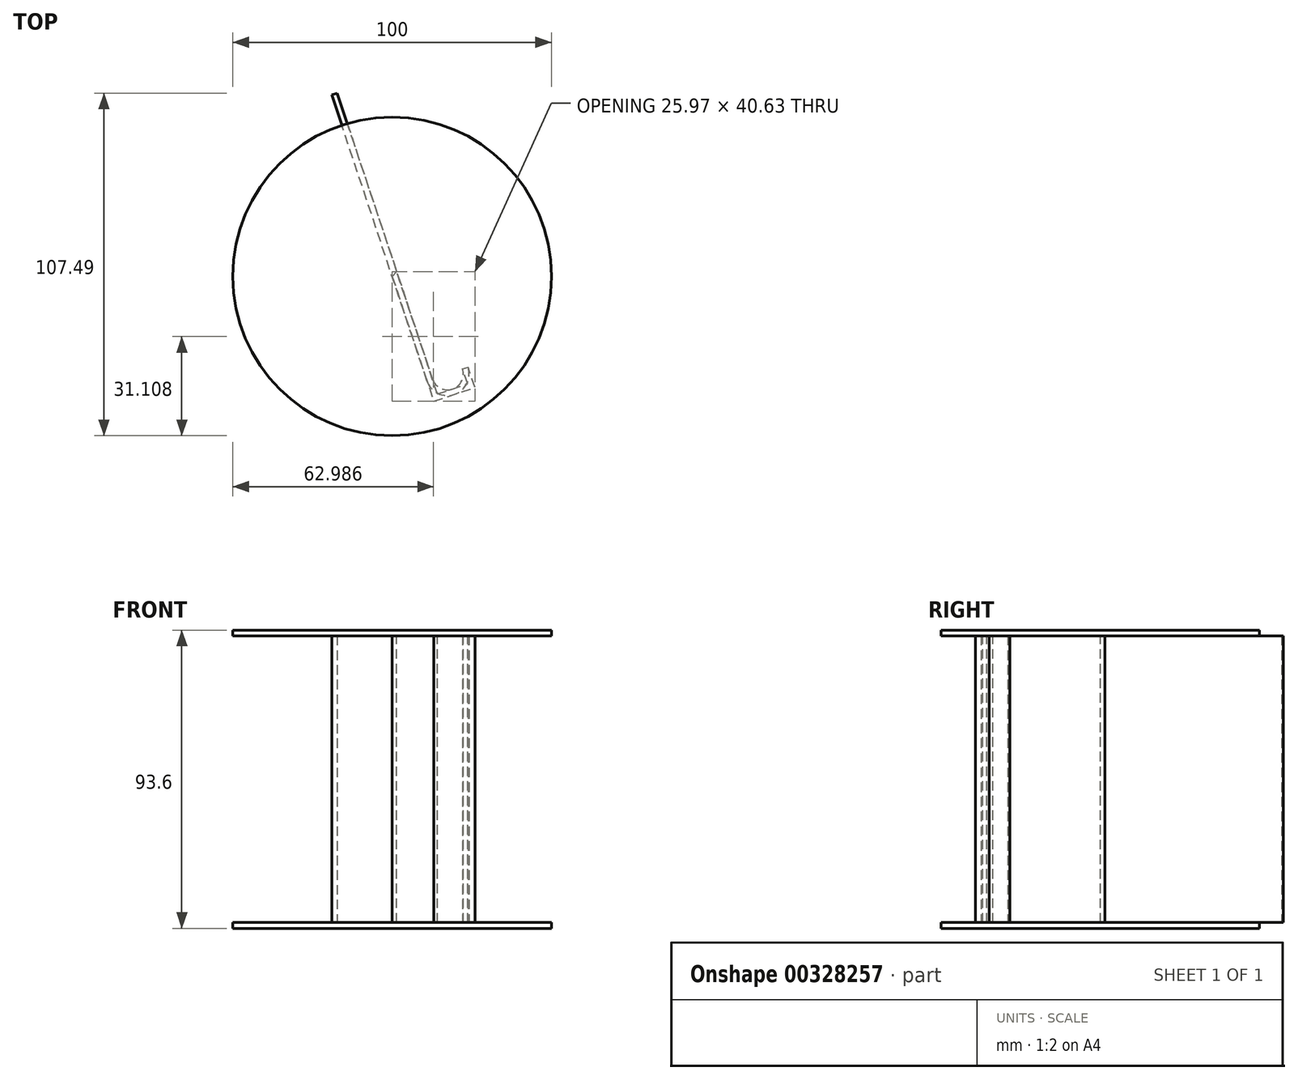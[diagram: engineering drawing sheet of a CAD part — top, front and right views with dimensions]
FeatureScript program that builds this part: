
annotation { "Feature Type Name" : "Feature", "Feature Type Description" : "" }
export const myFeature = defineFeature(function(context is Context, id is Id, definition is map)
    precondition{}
    {
        {
            var Q0;
            Q0=qCreatedBy(makeId("Top.planeOp"),FACE);
            var sketch = newSketch(context, id + "F0", { "sketchPlane" : qUnion([Q0])});
            skCircle(sketch, "E0", {"center": v(0, 0) * mm, "radius": 50 * mm});
            skLineSegment(sketch, "E1", {"start": v(0, -50) * mm, "end": v(50, 0) * mm});
            skLineSegment(sketch, "E2", {"start": v(25, -25) * mm, "end": v(0, -50) * mm});
            skLineSegment(sketch, "E3", {"start": v(12.5, -37.5) * mm, "end": v(0, 0) * mm});
            skLineSegment(sketch, "E4", {"start": v(-50, 0) * mm, "end": v(0, -50) * mm});
            skLineSegment(sketch, "E5", {"start": v(50, 0) * mm, "end": v(0, 50) * mm});
            skLineSegment(sketch, "E6", {"start": v(-25, -25) * mm, "end": v(25, 25) * mm});
            skLineSegment(sketch, "E7", {"start": v(25, 25) * mm, "end": v(0, 0) * mm});
            skLineSegment(sketch, "E8", {"start": v(25, 25) * mm, "end": v(12.5, 12.5) * mm});
            skLineSegment(sketch, "E9", {"start": v(0, 0) * mm, "end": v(1.27, 1.27) * mm});
            skLineSegment(sketch, "E10", {"start": v(12.5, -37.5) * mm, "end": v(13.77, -36.23) * mm});
            skLineSegment(sketch, "E11", {"start": v(12.5, -37.5) * mm, "end": v(14.2, -36.93) * mm});
            skLineSegment(sketch, "E12", {"start": v(0, 0) * mm, "end": v(1.7, 0.57) * mm});
            skLineSegment(sketch, "E13", {"start": v(1.7, 0.57) * mm, "end": v(14.2, -36.93) * mm});
            skLineSegment(sketch, "E14", {"start": v(1.7, 0.57) * mm, "end": v(1.42, 1.42) * mm});
            skLineSegment(sketch, "E15", {"start": v(14.2, -36.93) * mm, "end": v(23.7, -33.77) * mm});
            skLineSegment(sketch, "E16", {"start": v(12.5, -37.5) * mm, "end": v(13.07, -39.2) * mm});
            skLineSegment(sketch, "E17", {"start": v(13.07, -39.2) * mm, "end": v(24.26, -35.48) * mm});
            skLineSegment(sketch, "E18", {"start": v(23.7, -33.77) * mm, "end": v(24.26, -35.48) * mm});
            skLineSegment(sketch, "E19", {"start": v(24.26, -35.48) * mm, "end": v(25.97, -34.9) * mm});
            skLineSegment(sketch, "E20", {"start": v(25.97, -34.9) * mm, "end": v(23.82, -28.46) * mm});
            skLineSegment(sketch, "E21", {"start": v(23.7, -33.77) * mm, "end": v(22.11, -29.03) * mm});
            skLineSegment(sketch, "E22", {"start": v(22.11, -29.03) * mm, "end": v(23.82, -28.46) * mm});
            skLineSegment(sketch, "E23", {"start": v(23.7, -33.77) * mm, "end": v(25.4, -33.2) * mm});
            skLineSegment(sketch, "E24", {"start": v(0, 0) * mm, "end": v(-18.97, 56.92) * mm});
            skLineSegment(sketch, "E25", {"start": v(-18.97, 56.92) * mm, "end": v(-17.27, 57.5) * mm});
            skLineSegment(sketch, "E26", {"start": v(-17.27, 57.5) * mm, "end": v(1.42, 1.42) * mm});
            skSolve(sketch);
        }
        {
            var Q0;
            {var subQ0=sQuery(id+"F0.wireOp",EDGE,"E5");var subQ1=sQuery(id+"F0.wireOp",EDGE,"E0");var subQ3=makeQuery(id+"F0.imprint","INTERSECT",VERTEX,{"derivedFrom":[subQ1,subQ0]});Q0=makeQuery(id+"F0.imprint","IMPRINT",FACE,{"disambiguationData":[TD([[makeQuery(id+"F0.imprint","IMPRINT",EDGE,{"disambiguationData":[TD([[subQ3,1.0]])],"derivedFrom":subQ0}),-1.0]])]});}
            var Q1;
            {var subQ7=sQuery(id+"F0.wireOp",EDGE,"E14");Q1=makeQuery(id+"F0.imprint","IMPRINT",FACE,{"disambiguationData":[TD([[makeQuery(id+"F0.imprint","IMPRINT",EDGE,{"derivedFrom":subQ7}),-1.0]])]});}
            var Q2;
            {var subQ1=sQuery(id+"F0.wireOp",EDGE,"E6");var subQ3=makeQuery(id+"F0.imprint","IMPRINT",VERTEX,{"disambiguationData":[OD(0.0)],"derivedFrom":subQ1});Q2=makeQuery(id+"F0.imprint","IMPRINT",FACE,{"disambiguationData":[TD([[makeQuery(id+"F0.imprint","IMPRINT",EDGE,{"disambiguationData":[TD([[subQ3,-1.0]])],"derivedFrom":subQ1}),1.0]])]});}
            var Q3;
            {var subQ7=sQuery(id+"F0.wireOp",EDGE,"E15");Q3=makeQuery(id+"F0.imprint","IMPRINT",FACE,{"disambiguationData":[TD([[makeQuery(id+"F0.imprint","IMPRINT",EDGE,{"derivedFrom":subQ7}),1.0]])]});}
            var Q4;
            Q4=makeQuery(id+"F0.imprint","IMPRINT",FACE,{"disambiguationData":[TD([[makeQuery(id+"F0.imprint","IMPRINT",EDGE,{"derivedFrom":sQuery(id+"F0.wireOp",EDGE,"E21")}),-1.0]])]});
            var Q5;
            Q5=makeQuery(id+"F0.imprint","IMPRINT",FACE,{"disambiguationData":[TD([[makeQuery(id+"F0.imprint","IMPRINT",EDGE,{"derivedFrom":sQuery(id+"F0.wireOp",EDGE,"E18")}),1.0]])]});
            var Q6;
            Q6=makeQuery(id+"F0.imprint","IMPRINT",FACE,{"disambiguationData":[TD([[makeQuery(id+"F0.imprint","IMPRINT",EDGE,{"derivedFrom":sQuery(id+"F0.wireOp",EDGE,"E11")}),-1.0]])]});
            var Q7;
            {var subQ1=sQuery(id+"F0.wireOp",EDGE,"E3");Q7=makeQuery(id+"F0.imprint","IMPRINT",FACE,{"disambiguationData":[TD([[makeQuery(id+"F0.imprint","IMPRINT",EDGE,{"derivedFrom":subQ1}),-1.0]])]});}
            var Q8;
            {var subQ0=sQuery(id+"F0.wireOp",EDGE,"E11");Q8=makeQuery(id+"F0.imprint","IMPRINT",FACE,{"disambiguationData":[TD([[makeQuery(id+"F0.imprint","IMPRINT",EDGE,{"derivedFrom":subQ0}),1.0]])]});}
            var Q9;
            {var subQ0=sQuery(id+"F0.wireOp",EDGE,"E3");Q9=makeQuery(id+"F0.imprint","IMPRINT",FACE,{"disambiguationData":[TD([[makeQuery(id+"F0.imprint","IMPRINT",EDGE,{"derivedFrom":subQ0}),1.0]])]});}
            var Q10;
            {var subQ3=sQuery(id+"F0.wireOp",EDGE,"E0");var subQ5=sQuery(id+"F0.wireOp",EDGE,"E26");var subQ8=makeQuery(id+"F0.imprint","INTERSECT",VERTEX,{"derivedFrom":[subQ3,subQ5]});Q10=makeQuery(id+"F0.imprint","IMPRINT",FACE,{"disambiguationData":[TD([[makeQuery(id+"F0.imprint","IMPRINT",EDGE,{"disambiguationData":[TD([[subQ8,-1.0]])],"derivedFrom":subQ3}),1.0]])]});}
            var Q11;
            {var subQ0=sQuery(id+"F0.wireOp",EDGE,"E12");Q11=makeQuery(id+"F0.imprint","IMPRINT",FACE,{"disambiguationData":[TD([[makeQuery(id+"F0.imprint","IMPRINT",EDGE,{"derivedFrom":subQ0}),1.0]])]});}
            var Q12;
            {var subQ0=sQuery(id+"F0.wireOp",EDGE,"E4");var subQ1=sQuery(id+"F0.wireOp",EDGE,"E0");var subQ2=makeQuery(id+"F0.imprint","INTERSECT",VERTEX,{"derivedFrom":[subQ1,subQ0]});Q12=makeQuery(id+"F0.imprint","IMPRINT",FACE,{"disambiguationData":[TD([[makeQuery(id+"F0.imprint","IMPRINT",EDGE,{"disambiguationData":[TD([[subQ2,1.0]])],"derivedFrom":subQ1}),1.0]])]});}
            var Q13;
            {var subQ0=sQuery(id+"F0.wireOp",EDGE,"E4");var subQ1=sQuery(id+"F0.wireOp",EDGE,"E0");var subQ2=makeQuery(id+"F0.imprint","INTERSECT",VERTEX,{"derivedFrom":[subQ1,subQ0]});Q13=makeQuery(id+"F0.imprint","IMPRINT",FACE,{"disambiguationData":[TD([[makeQuery(id+"F0.imprint","IMPRINT",EDGE,{"disambiguationData":[TD([[subQ2,-1.0]])],"derivedFrom":subQ0}),-1.0]])]});}
            extrude(context, id + "F1", {"entities" : qUnion([Q0, Q1, Q2, Q3, Q4, Q5, Q6, Q7, Q8, Q9, Q10, Q11, Q12, Q13]), "depth" : (45 + 1.8) * mm, "offsetDistance" : 25 * mm, "hasSecondDirection" : true, "secondDirectionOppositeDirection" : true, "secondDirectionDepth" : 46.8 * mm});
        }
        {
            var Q0;
            {var subQ0=sQuery(id+"F0.wireOp",EDGE,"E4");var subQ1=sQuery(id+"F0.wireOp",EDGE,"E0");var subQ2=makeQuery(id+"F0.imprint","INTERSECT",VERTEX,{"derivedFrom":[subQ1,subQ0]});var subQ5=sQuery(id+"F0.wireOp",EDGE,"E6");var subQ7=makeQuery(id+"F0.imprint","IMPRINT",EDGE,{"disambiguationData":[TD([[subQ2,-1.0]])],"derivedFrom":subQ0});var subQ12=sQuery(id+"F0.wireOp",EDGE,"E3");var subQ16=sQuery(id+"F0.wireOp",EDGE,"E5");var subQ18=makeQuery(id+"F0.imprint","INTERSECT",VERTEX,{"derivedFrom":[subQ1,subQ16]});var subQ20=makeQuery(id+"F0.imprint","IMPRINT",EDGE,{"disambiguationData":[TD([[subQ18,1.0]])],"derivedFrom":subQ16});var subQ32=sQuery(id+"F0.wireOp",EDGE,"E15");var subQ35=sQuery(id+"F0.wireOp",EDGE,"E26");var subQ36=sQuery(id+"F0.wireOp",EDGE,"E14");var subQ38=makeQuery(id+"F0.imprint","IMPRINT",VERTEX,{"disambiguationData":[OD(0.0)],"derivedFrom":subQ5});var subQ40=makeQuery(id+"F0.imprint","IMPRINT",EDGE,{"disambiguationData":[TD([[subQ38,-1.0]])],"derivedFrom":subQ5});var subQ41=makeQuery(id+"F0.imprint","INTERSECT",VERTEX,{"derivedFrom":[subQ1,subQ35]});var subQ43=makeQuery(id+"F0.imprint","IMPRINT",EDGE,{"disambiguationData":[TD([[subQ41,-1.0]])],"derivedFrom":subQ1});var subQ44=sQuery(id+"F0.wireOp",EDGE,"E25");Q0=qUnion([makeQuery(id+"F0.imprint","IMPRINT",FACE,{"disambiguationData":[TD([[makeQuery(id+"F0.imprint","IMPRINT",EDGE,{"derivedFrom":subQ36}),-1.0]])]}),makeQuery(id+"F0.imprint","IMPRINT",FACE,{"disambiguationData":[TD([[subQ43,1.0]])]}),makeQuery(id+"F0.imprint","IMPRINT",FACE,{"disambiguationData":[TD([[makeQuery(id+"F0.imprint","IMPRINT",EDGE,{"derivedFrom":subQ44}),-1.0]])]}),makeQuery(id+"F0.imprint","IMPRINT",FACE,{"disambiguationData":[TD([[subQ40,1.0]])]}),makeQuery(id+"F0.imprint","IMPRINT",FACE,{"disambiguationData":[TD([[makeQuery(id+"F0.imprint","IMPRINT",EDGE,{"derivedFrom":subQ32}),1.0]])]}),makeQuery(id+"F0.imprint","IMPRINT",FACE,{"disambiguationData":[TD([[makeQuery(id+"F0.imprint","IMPRINT",EDGE,{"derivedFrom":subQ12}),1.0]])]}),makeQuery(id+"F0.imprint","IMPRINT",FACE,{"disambiguationData":[TD([[subQ20,-1.0]])]}),makeQuery(id+"F0.imprint","IMPRINT",FACE,{"disambiguationData":[TD([[makeQuery(id+"F0.imprint","IMPRINT",EDGE,{"disambiguationData":[TD([[subQ2,1.0]])],"derivedFrom":subQ1}),1.0]])]}),makeQuery(id+"F0.imprint","IMPRINT",FACE,{"disambiguationData":[TD([[subQ7,-1.0]])]})]);}
            extrude(context, id + "F2", {"entities" : qUnion([Q0]), "operationType" : NewBodyOperationType.REMOVE, "oppositeDirection" : true, "depth" : 45 * mm, "offsetDistance" : 25 * mm, "hasSecondDirection" : true, "secondDirectionOppositeDirection" : false, "secondDirectionDepth" : 45 * mm});
        }
        {
            var Q0;
            Q0=qCreatedBy(makeId("Front.planeOp"),FACE);
            var Q1;
            Q1=qCreatedBy(makeId("Right.planeOp"),FACE);
            cPlane(context, id + "F3", {"entities" : qUnion([Q0, Q1]), "cplaneType" : CPlaneType.MID_PLANE, "offset" : 25 * mm, "width" : 150 * mm, "height" : 150 * mm});
        }
        {
            var Q0;
            {var subQ5=sQuery(id+"F0.wireOp",EDGE,"E25");Q0=makeQuery(id+"F0.imprint","IMPRINT",FACE,{"disambiguationData":[TD([[makeQuery(id+"F0.imprint","IMPRINT",EDGE,{"derivedFrom":subQ5}),-1.0]])]});}
            var Q1;
            {var subQ3=sQuery(id+"F0.wireOp",EDGE,"E0");var subQ5=sQuery(id+"F0.wireOp",EDGE,"E26");var subQ8=makeQuery(id+"F0.imprint","INTERSECT",VERTEX,{"derivedFrom":[subQ3,subQ5]});Q1=makeQuery(id+"F0.imprint","IMPRINT",FACE,{"disambiguationData":[TD([[makeQuery(id+"F0.imprint","IMPRINT",EDGE,{"disambiguationData":[TD([[subQ8,-1.0]])],"derivedFrom":subQ3}),1.0]])]});}
            var Q2;
            {var subQ0=sQuery(id+"F0.wireOp",EDGE,"E12");Q2=makeQuery(id+"F0.imprint","IMPRINT",FACE,{"disambiguationData":[TD([[makeQuery(id+"F0.imprint","IMPRINT",EDGE,{"derivedFrom":subQ0}),1.0]])]});}
            var Q3;
            {var subQ1=sQuery(id+"F0.wireOp",EDGE,"E3");Q3=makeQuery(id+"F0.imprint","IMPRINT",FACE,{"disambiguationData":[TD([[makeQuery(id+"F0.imprint","IMPRINT",EDGE,{"derivedFrom":subQ1}),-1.0]])]});}
            var Q4;
            {var subQ0=sQuery(id+"F0.wireOp",EDGE,"E11");Q4=makeQuery(id+"F0.imprint","IMPRINT",FACE,{"disambiguationData":[TD([[makeQuery(id+"F0.imprint","IMPRINT",EDGE,{"derivedFrom":subQ0}),1.0]])]});}
            var Q5;
            Q5=makeQuery(id+"F0.imprint","IMPRINT",FACE,{"disambiguationData":[TD([[makeQuery(id+"F0.imprint","IMPRINT",EDGE,{"derivedFrom":sQuery(id+"F0.wireOp",EDGE,"E11")}),-1.0]])]});
            var Q6;
            Q6=makeQuery(id+"F0.imprint","IMPRINT",FACE,{"disambiguationData":[TD([[makeQuery(id+"F0.imprint","IMPRINT",EDGE,{"derivedFrom":sQuery(id+"F0.wireOp",EDGE,"E18")}),1.0]])]});
            var Q7;
            Q7=makeQuery(id+"F0.imprint","IMPRINT",FACE,{"disambiguationData":[TD([[makeQuery(id+"F0.imprint","IMPRINT",EDGE,{"derivedFrom":sQuery(id+"F0.wireOp",EDGE,"E21")}),-1.0]])]});
            extrude(context, id + "F4", {"entities" : qUnion([Q0, Q1, Q2, Q3, Q4, Q5, Q6, Q7]), "depth" : 45 * mm, "offsetDistance" : 25 * mm, "hasSecondDirection" : true, "secondDirectionOppositeDirection" : true, "secondDirectionDepth" : 45 * mm});
        }
        {
            var Q0;
            Q0=makeQuery(id+"F4.opExtrude","SWEPT_EDGE",EDGE,{"disambiguationData":[OSD([sQuery(id+"F0.wireOp",EDGE,"E15"),sQuery(id+"F0.wireOp",EDGE,"E18"),sQuery(id+"F0.wireOp",EDGE,"E21"),sQuery(id+"F0.wireOp",EDGE,"E23")])]});
            var Q1;
            Q1=makeQuery(id+"F4.opExtrude","SWEPT_EDGE",EDGE,{"disambiguationData":[OSD([sQuery(id+"F0.wireOp",EDGE,"E11"),sQuery(id+"F0.wireOp",EDGE,"E13"),sQuery(id+"F0.wireOp",EDGE,"E15")])]});
            fillet(context, id + "F5", {"entities" : qUnion([Q0, Q1]), "radius" : 5 * mm, "tangentPropagation" : true, "allowEdgeOverflow" : false});
        }
        {
            var Q0;
            Q0=makeQuery(id+"F4.opExtrude","SWEPT_EDGE",EDGE,{"disambiguationData":[OSD([sQuery(id+"F0.wireOp",EDGE,"E19"),sQuery(id+"F0.wireOp",EDGE,"E20")])]});
            var Q1;
            Q1=makeQuery(id+"F4.opExtrude","SWEPT_EDGE",EDGE,{"disambiguationData":[OSD([sQuery(id+"F0.wireOp",EDGE,"E16"),sQuery(id+"F0.wireOp",EDGE,"E17")])]});
            fillet(context, id + "F6", {"entities" : qUnion([Q0, Q1]), "radius" : 6.8 * mm, "tangentPropagation" : true, "allowEdgeOverflow" : false});
        }
    });
